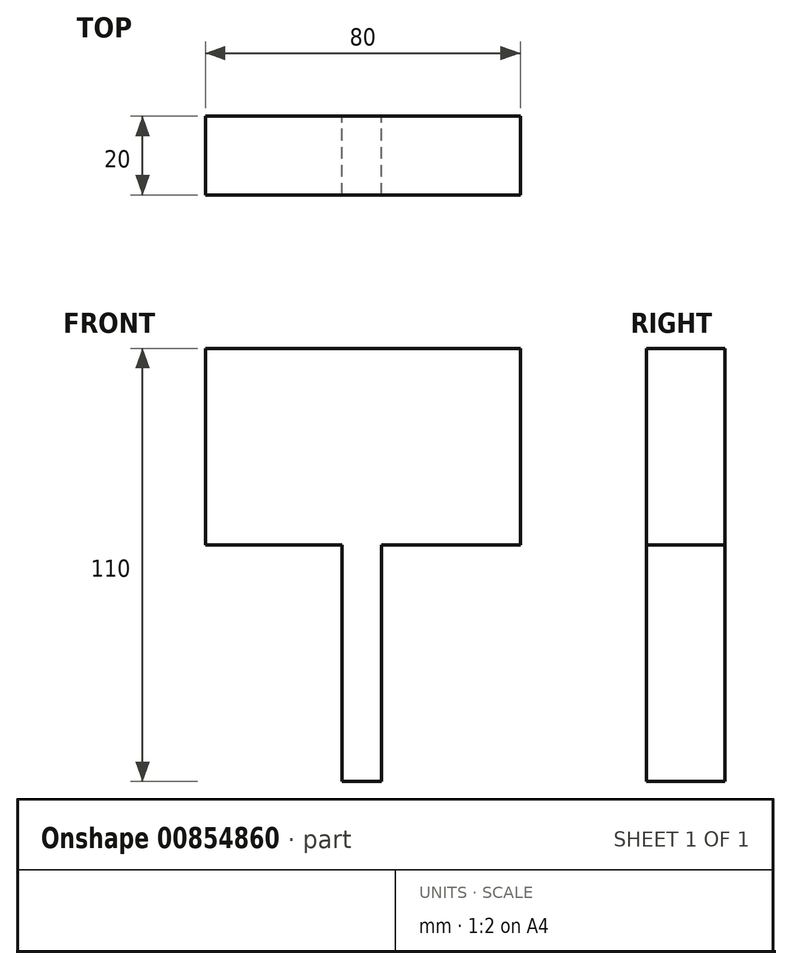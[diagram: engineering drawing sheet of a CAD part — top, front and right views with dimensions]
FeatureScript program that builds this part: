
annotation { "Feature Type Name" : "Feature", "Feature Type Description" : "" }
export const myFeature = defineFeature(function(context is Context, id is Id, definition is map)
    precondition{}
    {
        {
            var Q0;
            Q0=qCreatedBy(makeId("Front.planeOp"),FACE);
            var sketch = newSketch(context, id + "F0", { "sketchPlane" : qUnion([Q0])});
            skLineSegment(sketch, "E0.bottom", {"start": v(-40, 25) * mm, "end": v(40, 25) * mm});
            skLineSegment(sketch, "E0.top", {"start": v(-40, -25) * mm, "end": v(40, -25) * mm});
            skLineSegment(sketch, "E0.left", {"start": v(-40, 25) * mm, "end": v(-40, -25) * mm});
            skLineSegment(sketch, "E0.right", {"start": v(40, 25) * mm, "end": v(40, -25) * mm});
            skPoint(sketch, "E0.middle", {"position": v(0, 0) * mm});
            skLineSegment(sketch, "E1.bottom", {"start": v(-5.24, -25) * mm, "end": v(4.76, -25) * mm});
            skLineSegment(sketch, "E1.top", {"start": v(-5.24, -85) * mm, "end": v(4.76, -85) * mm});
            skLineSegment(sketch, "E1.left", {"start": v(-5.24, -25) * mm, "end": v(-5.24, -85) * mm});
            skLineSegment(sketch, "E1.right", {"start": v(4.76, -25) * mm, "end": v(4.76, -85) * mm});
            skSolve(sketch);
        }
        {
            var Q0;
            Q0 = qSketchRegion(id + "F0", true);
            extrude(context, id + "F1", {"entities" : qUnion([Q0]), "depth" : 20 * mm, "offsetDistance" : 25.4 * mm});
        }
    });
